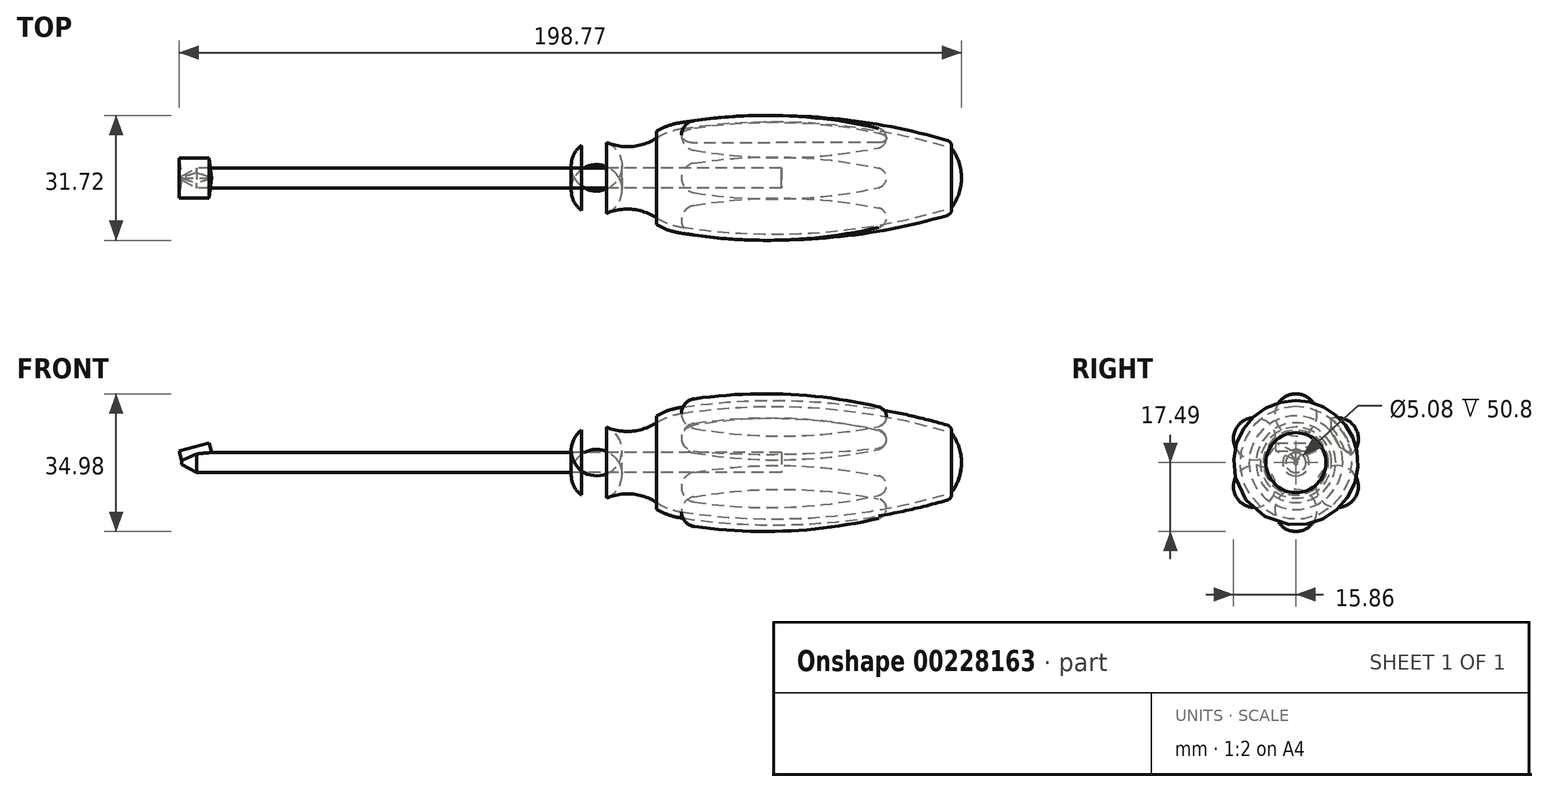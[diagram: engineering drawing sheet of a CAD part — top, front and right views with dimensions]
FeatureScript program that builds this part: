
annotation { "Feature Type Name" : "Feature", "Feature Type Description" : "" }
export const myFeature = defineFeature(function(context is Context, id is Id, definition is map)
    precondition{}
    {
        {
            var Q0;
            Q0=qCreatedBy(makeId("Front.planeOp"),FACE);
            var sketch = newSketch(context, id + "F0", { "sketchPlane" : qUnion([Q0])});
            skLineSegment(sketch, "E0", {"start": v(-101.6, 0) * mm, "end": v(96.52, 0) * mm});
            skLineSegment(sketch, "E1", {"start": v(96.52, 0) * mm, "end": v(117.55, 0) * mm, "construction": true});
            skLineSegment(sketch, "E2", {"start": v(50.8, 2.54) * mm, "end": v(-97.8, 2.54) * mm});
            skLineSegment(sketch, "E3", {"start": v(-101.6, 0.5) * mm, "end": v(-101.6, 0) * mm});
            skLineSegment(sketch, "E4", {"start": v(0, 2.54) * mm, "end": v(0, 8.25) * mm});
            skArc(sketch, "E5", {"start": v(6.35, 9.02) * mm, "mid": v(3.07, 9.48) * mm, "end": v(0, 8.25) * mm});
            skArc(sketch, "E6", {"start": v(6.35, 9.02) * mm, "mid": v(12.84, 7.99) * mm, "end": v(19.05, 10.11) * mm});
            skArc(sketch, "E7", {"start": v(25.4, 12.52) * mm, "mid": v(22.1, 11.65) * mm, "end": v(19.05, 10.11) * mm});
            skArc(sketch, "E8", {"start": v(93.98, 7.62) * mm, "mid": v(59.96, 13.9) * mm, "end": v(25.4, 12.52) * mm});
            skArc(sketch, "E9", {"start": v(96.52, 0) * mm, "mid": v(95.87, 4.02) * mm, "end": v(93.98, 7.62) * mm});
            skArc(sketch, "E10.0", {"start": v(25.17, 14.02) * mm, "mid": v(22.01, 13.24) * mm, "end": v(19.05, 11.9) * mm});
            skArc(sketch, "E10.1", {"start": v(92.95, 9.52) * mm, "mid": v(59.3, 15.46) * mm, "end": v(25.17, 14.02) * mm});
            skLineSegment(sketch, "E11", {"start": v(19.05, 11.9) * mm, "end": v(19.05, 10.11) * mm});
            skArc(sketch, "E12", {"start": v(93.98, 7.62) * mm, "mid": v(93.86, 8.78) * mm, "end": v(92.95, 9.52) * mm});
            skPoint(sketch, "E13.orphan", {"position": v(0, 0) * mm});
            skLineSegment(sketch, "E14", {"start": v(50.8, 2.54) * mm, "end": v(50.8, 0) * mm});
            skLineSegment(sketch, "E15", {"start": v(-101.6, 0.5) * mm, "end": v(-97.8, 2.54) * mm});
            skPoint(sketch, "E16.orphan", {"position": v(-101.6, 2.54) * mm});
            skSolve(sketch);
        }
        {
            var Q0;
            Q0=qCreatedBy(makeId("Front.planeOp"),FACE);
            var sketch = newSketch(context, id + "F1", { "sketchPlane" : qUnion([Q0])});
            skLineSegment(sketch, "E17", {"start": v(25.4, 12.52) * mm, "end": v(77.47, 11.64) * mm});
            skArc(sketch, "E18", {"start": v(28.67, 16.22) * mm, "mid": v(26.35, 14.97) * mm, "end": v(25.4, 12.52) * mm});
            skArc(sketch, "E19", {"start": v(77.47, 11.64) * mm, "mid": v(76.93, 13.25) * mm, "end": v(75.5, 14.16) * mm});
            skArc(sketch, "E20", {"start": v(75.5, 14.16) * mm, "mid": v(52.19, 17.37) * mm, "end": v(28.67, 16.22) * mm});
            skSolve(sketch);
        }
        {
            var Q0;
            Q0=qCreatedBy(makeId("Front.planeOp"),FACE);
            var sketch = newSketch(context, id + "F2", { "sketchPlane" : qUnion([Q0])});
            skLineSegment(sketch, "E21", {"start": v(-101.6, 0.5) * mm, "end": v(-93.98, 2.54) * mm});
            skSolve(sketch);
        }
        {
            var Q0;
            Q0=sQuery(id+"F2.wireOp",VERTEX,"E21.start");
            var Q1;
            Q1=sQuery(id+"F2.wireOp",EDGE,"E21");
            cPlane(context, id + "F3", {"entities" : qUnion([Q0, Q1]), "cplaneType" : CPlaneType.LINE_POINT, "offset" : 25.4 * mm, "width" : 152.4 * mm, "height" : 152.4 * mm});
        }
        {
            var Q0;
            Q0=qCreatedBy(id+"F3.planeOp",FACE);
            var sketch = newSketch(context, id + "F4", { "sketchPlane" : qUnion([Q0])});
            skLineSegment(sketch, "E22", {"start": v(5.08, 29.2) * mm, "end": v(0, 26.67) * mm});
            skLineSegment(sketch, "E23", {"start": v(0, 26.67) * mm, "end": v(-5.08, 29.2) * mm});
            skLineSegment(sketch, "E24", {"start": v(-5.08, 29.2) * mm, "end": v(5.08, 29.2) * mm});
            skLineSegment(sketch, "E25", {"start": v(0, 29.2) * mm, "end": v(0, 26.67) * mm, "construction": true});
            skSolve(sketch);
        }
        {
            var Q0;
            {var subQ0=sQuery(id+"F0.wireOp",EDGE,"E3");Q0=makeQuery(id+"F0.imprint","IMPRINT",FACE,{"disambiguationData":[TD([[makeQuery(id+"F0.imprint","IMPRINT",EDGE,{"derivedFrom":subQ0}),1.0]])]});}
            var Q1;
            Q1=sQuery(id+"F0.wireOp",EDGE,"E1");
            revolve(context, id + "F5", {"entities" : qUnion([Q0]), "axis" : qUnion([Q1]), "revolveType" : RevolveType.FULL});
        }
        {
            var Q0;
            {var subQ0=sQuery(id+"F0.wireOp",EDGE,"E4");Q0=makeQuery(id+"F0.imprint","IMPRINT",FACE,{"disambiguationData":[TD([[makeQuery(id+"F0.imprint","IMPRINT",EDGE,{"derivedFrom":subQ0}),-1.0]])]});}
            var Q1;
            Q1=sQuery(id+"F0.wireOp",EDGE,"E1");
            revolve(context, id + "F6", {"entities" : qUnion([Q0]), "axis" : qUnion([Q1]), "revolveType" : RevolveType.FULL});
        }
        {
            var Q0;
            Q0=makeQuery(id+"F0.imprint","IMPRINT",FACE,{"disambiguationData":[TD([[makeQuery(id+"F0.imprint","IMPRINT",EDGE,{"derivedFrom":sQuery(id+"F0.wireOp",EDGE,"E7")}),-1.0]])]});
            var Q1;
            Q1=sQuery(id+"F0.wireOp",EDGE,"E1");
            revolve(context, id + "F7", {"entities" : qUnion([Q0]), "axis" : qUnion([Q1]), "revolveType" : RevolveType.FULL});
        }
        {
            var Q0;
            Q0=makeQuery(id+"F1.imprint","IMPRINT",FACE,{"disambiguationData":[TD([[makeQuery(id+"F1.imprint","IMPRINT",EDGE,{"derivedFrom":sQuery(id+"F1.wireOp",EDGE,"E17")}),1.0]])]});
            var Q1;
            Q1=sQuery(id+"F1.wireOp",EDGE,"E17");
            revolve(context, id + "F8", {"entities" : qUnion([Q0]), "axis" : qUnion([Q1]), "revolveType" : RevolveType.FULL});
        }
        {
            var Q0;
            Q0=makeQuery(id+"F8.opRevolve","SWEPT_BODY",BODY,{"disambiguationData":[OSD([sQuery(id+"F1.wireOp",EDGE,"E17"),sQuery(id+"F1.wireOp",EDGE,"E18"),sQuery(id+"F1.wireOp",EDGE,"E19"),sQuery(id+"F1.wireOp",EDGE,"E20")])]});
            var Q1;
            Q1=sQuery(id+"F0.wireOp",EDGE,"E1");
            circularPattern(context, id + "F9", {"entities" : qUnion([Q0]), "axis" : qUnion([Q1]), "angle" : 360 * degree, "instanceCount" : 6, "equalSpace" : true});
        }
        {
            var Q0;
            Q0=makeQuery(id+"F6.opRevolve","SWEPT_BODY",BODY,{"disambiguationData":[OSD([sQuery(id+"F0.wireOp",EDGE,"E0"),sQuery(id+"F0.wireOp",EDGE,"E2"),sQuery(id+"F0.wireOp",EDGE,"E4"),sQuery(id+"F0.wireOp",EDGE,"E5"),sQuery(id+"F0.wireOp",EDGE,"E6"),sQuery(id+"F0.wireOp",EDGE,"E7"),sQuery(id+"F0.wireOp",EDGE,"E8"),sQuery(id+"F0.wireOp",EDGE,"E9"),sQuery(id+"F0.wireOp",EDGE,"E14")])]});
            var Q1;
            Q1=makeQuery(id+"F9.opPattern","COPY",BODY,{"derivedFrom":makeQuery(id+"F8.opRevolve","SWEPT_BODY",BODY,{"disambiguationData":[OSD([sQuery(id+"F1.wireOp",EDGE,"E17"),sQuery(id+"F1.wireOp",EDGE,"E18"),sQuery(id+"F1.wireOp",EDGE,"E19"),sQuery(id+"F1.wireOp",EDGE,"E20")])]}),"instanceName":"5"});
            booleanBodies(context, id + "F10", {"operationType" : BooleanOperationType.SUBTRACTION, "tools" : qUnion([Q0]), "targets" : qUnion([Q1]), "keepTools" : true});
        }
        {
            var Q0;
            Q0=makeQuery(id+"F4.imprint","IMPRINT",FACE,{"disambiguationData":[TD([[makeQuery(id+"F4.imprint","IMPRINT",EDGE,{"derivedFrom":sQuery(id+"F4.wireOp",EDGE,"E22")}),-1.0]])]});
            var Q1;
            Q1=sQuery(id+"F2.wireOp",EDGE,"E21");
            sweep(context, id + "F11", {"operationType" : NewBodyOperationType.REMOVE, "profiles" : qUnion([Q0]), "path" : qUnion([Q1])});
        }
        {
            var Q0;
            Q0=makeQuery(id+"F4.imprint","IMPRINT",FACE,{"disambiguationData":[TD([[makeQuery(id+"F4.imprint","IMPRINT",EDGE,{"derivedFrom":sQuery(id+"F4.wireOp",EDGE,"E22")}),-1.0]])]});
            var Q1;
            Q1=qConstructionFilter(qBodyType(qCreatedBy(id+"F2",EDGE),BodyType.WIRE),ConstructionObject.NO);
            sweep(context, id + "F12", {"profiles" : qUnion([Q0]), "path" : qUnion([Q1])});
        }
    });
